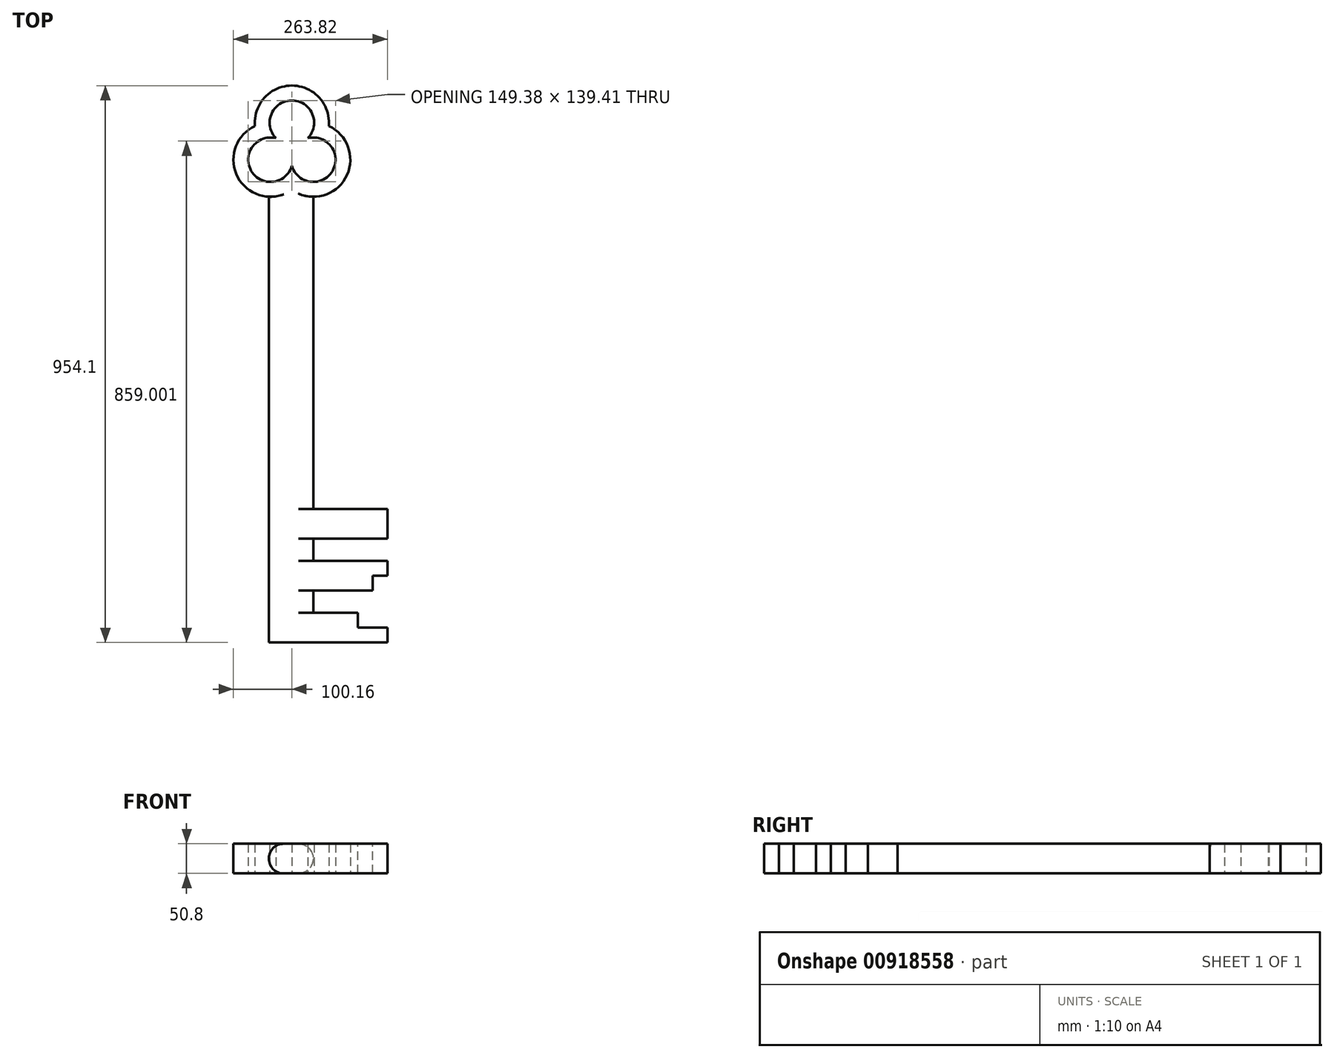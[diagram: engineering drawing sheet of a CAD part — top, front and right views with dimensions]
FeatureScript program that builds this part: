
annotation { "Feature Type Name" : "Feature", "Feature Type Description" : "" }
export const myFeature = defineFeature(function(context is Context, id is Id, definition is map)
    precondition{}
    {
        {
            var Q0;
            Q0=qCreatedBy(makeId("Top.planeOp"),FACE);
            var sketch = newSketch(context, id + "F0", { "sketchPlane" : qUnion([Q0])});
            skLineSegment(sketch, "E0.top", {"start": v(-125.96, -437.06) * mm, "end": v(-49.76, -437.06) * mm});
            skLineSegment(sketch, "E0.right", {"start": v(-49.76, 326.6) * mm, "end": v(-49.76, -208.46) * mm});
            skArc(sketch, "E1", {"start": v(-113.73, 426.98) * mm, "mid": v(-156.08, 371) * mm, "end": v(-86.42, 379.67) * mm});
            skArc(sketch, "E2", {"start": v(-86.42, 379.67) * mm, "mid": v(-16.76, 371) * mm, "end": v(-59.1, 426.98) * mm});
            skArc(sketch, "E3", {"start": v(-59.1, 426.98) * mm, "mid": v(-86.42, 491.64) * mm, "end": v(-113.73, 426.98) * mm});
            skLineSegment(sketch, "E4", {"start": v(-49.76, -437.06) * mm, "end": v(77.24, -437.06) * mm});
            skLineSegment(sketch, "E5", {"start": v(77.24, -437.06) * mm, "end": v(77.24, -386.26) * mm});
            skLineSegment(sketch, "E6", {"start": v(77.24, -386.26) * mm, "end": v(-49.76, -386.26) * mm});
            skLineSegment(sketch, "E7", {"start": v(-49.76, -348.16) * mm, "end": v(77.24, -348.16) * mm});
            skLineSegment(sketch, "E8", {"start": v(77.24, -348.16) * mm, "end": v(77.24, -297.36) * mm});
            skLineSegment(sketch, "E9", {"start": v(77.24, -297.36) * mm, "end": v(-49.76, -297.36) * mm});
            skLineSegment(sketch, "E10", {"start": v(-49.76, -259.26) * mm, "end": v(77.24, -259.26) * mm});
            skLineSegment(sketch, "E11", {"start": v(77.24, -259.26) * mm, "end": v(77.24, -208.46) * mm});
            skLineSegment(sketch, "E12", {"start": v(77.24, -208.46) * mm, "end": v(-49.76, -208.46) * mm});
            skArc(sketch, "E13", {"start": v(-149.65, 447.72) * mm, "mid": v(-185.4, 377.85) * mm, "end": v(-125.96, 326.6) * mm});
            skArc(sketch, "E14", {"start": v(-49.76, 326.6) * mm, "mid": v(12.2, 376.45) * mm, "end": v(-23.2, 447.65) * mm});
            skLineSegment(sketch, "E15.trimOffspring", {"start": v(-125.96, 326.6) * mm, "end": v(-125.96, -437.06) * mm});
            skArc(sketch, "E16.trimOffspring", {"start": v(-23.2, 447.65) * mm, "mid": v(-86.39, 517.04) * mm, "end": v(-149.65, 447.72) * mm});
            skLineSegment(sketch, "E17.trimOffspring", {"start": v(-49.76, -259.26) * mm, "end": v(-49.76, -297.36) * mm});
            skLineSegment(sketch, "E18.trimOffspring", {"start": v(-49.76, -348.16) * mm, "end": v(-49.76, -386.26) * mm});
            skLineSegment(sketch, "E19", {"start": v(-125.96, 326.6) * mm, "end": v(-49.76, 326.6) * mm, "construction": true});
            skLineSegment(sketch, "E20", {"start": v(-123.08, 390.04) * mm, "end": v(-49.76, 390.04) * mm, "construction": true});
            skLineSegment(sketch, "E21", {"start": v(-123.08, 390.04) * mm, "end": v(-86.42, 453.54) * mm, "construction": true});
            skLineSegment(sketch, "E22", {"start": v(-49.76, 390.04) * mm, "end": v(-86.42, 453.54) * mm, "construction": true});
            skSolve(sketch);
        }
        {
            var Q0;
            Q0 = qSketchRegion(id + "F0", true);
            extrude(context, id + "F1", {"entities" : qUnion([Q0]), "depth" : 50.8 * mm, "offsetDistance" : 25.4 * mm});
        }
        {
            var Q0;
            Q0=makeQuery(id+"F1.opExtrude","CAP_EDGE",EDGE,{"disambiguationData":[OSD([sQuery(id+"F0.wireOp",EDGE,"E15.trimOffspring")])],"isStart":false});
            var Q1;
            Q1=makeQuery(id+"F1.opExtrude","CAP_EDGE",EDGE,{"disambiguationData":[OSD([sQuery(id+"F0.wireOp",EDGE,"E0.right")])],"isStart":false});
            var Q2;
            Q2=makeQuery(id+"F1.opExtrude","CAP_EDGE",EDGE,{"disambiguationData":[OSD([sQuery(id+"F0.wireOp",EDGE,"E0.right")])],"isStart":true});
            var Q3;
            Q3=makeQuery(id+"F1.opExtrude","CAP_EDGE",EDGE,{"disambiguationData":[OSD([sQuery(id+"F0.wireOp",EDGE,"E15.trimOffspring")])],"isStart":true});
            var Q4;
            Q4=makeQuery(id+"F1.opExtrude","CAP_EDGE",EDGE,{"disambiguationData":[OSD([sQuery(id+"F0.wireOp",EDGE,"E17.trimOffspring")])],"isStart":true});
            var Q5;
            Q5=makeQuery(id+"F1.opExtrude","CAP_EDGE",EDGE,{"disambiguationData":[OSD([sQuery(id+"F0.wireOp",EDGE,"E18.trimOffspring")])],"isStart":true});
            var Q6;
            Q6=makeQuery(id+"F1.opExtrude","CAP_EDGE",EDGE,{"disambiguationData":[OSD([sQuery(id+"F0.wireOp",EDGE,"E18.trimOffspring")])],"isStart":false});
            var Q7;
            Q7=makeQuery(id+"F1.opExtrude","CAP_EDGE",EDGE,{"disambiguationData":[OSD([sQuery(id+"F0.wireOp",EDGE,"E17.trimOffspring")])],"isStart":false});
            fillet(context, id + "F2", {"entities" : qUnion([Q0, Q1, Q2, Q3, Q4, Q5, Q6, Q7]), "radius" : 25.4 * mm, "tangentPropagation" : true, "allowEdgeOverflow" : false});
        }
        {
            var Q0;
            Q0=makeQuery(id+"F1.opExtrude","CAP_FACE",FACE,{"disambiguationData":[OSD([sQuery(id+"F0.wireOp",EDGE,"E0.top"),sQuery(id+"F0.wireOp",EDGE,"E0.right"),sQuery(id+"F0.wireOp",EDGE,"E1"),sQuery(id+"F0.wireOp",EDGE,"E2"),sQuery(id+"F0.wireOp",EDGE,"E3"),sQuery(id+"F0.wireOp",EDGE,"E4"),sQuery(id+"F0.wireOp",EDGE,"E5"),sQuery(id+"F0.wireOp",EDGE,"E6"),sQuery(id+"F0.wireOp",EDGE,"E7"),sQuery(id+"F0.wireOp",EDGE,"E8"),sQuery(id+"F0.wireOp",EDGE,"E9"),sQuery(id+"F0.wireOp",EDGE,"E10"),sQuery(id+"F0.wireOp",EDGE,"E11"),sQuery(id+"F0.wireOp",EDGE,"E12"),sQuery(id+"F0.wireOp",EDGE,"E13"),sQuery(id+"F0.wireOp",EDGE,"E14"),sQuery(id+"F0.wireOp",EDGE,"E15.trimOffspring"),sQuery(id+"F0.wireOp",EDGE,"E16.trimOffspring"),sQuery(id+"F0.wireOp",EDGE,"E17.trimOffspring"),sQuery(id+"F0.wireOp",EDGE,"E18.trimOffspring")])],"isStart":false});
            var sketch = newSketch(context, id + "F3", { "sketchPlane" : qUnion([Q0])});
            skSolve(sketch);
        }
        {
            var Q0;
            {var subQ17=sQuery(id+"F0.wireOp",EDGE,"E1");Q0=makeQuery(id+"F3.imprint","IMPRINT",FACE,{"disambiguationData":[TD([[makeQuery(id+"F3.imprint","IMPRINT",EDGE,{"derivedFrom":makeQuery(id+"F1.opExtrude","CAP_EDGE",EDGE,{"disambiguationData":[OSD([subQ17])],"isStart":false})}),-1.0]])]});}
            var sketch = newSketch(context, id + "F4", { "sketchPlane" : qUnion([Q0])});
            skLineSegment(sketch, "E23.bottom", {"start": v(26.44, -411.66) * mm, "end": v(88.26, -411.66) * mm});
            skLineSegment(sketch, "E23.top", {"start": v(26.44, -369.46) * mm, "end": v(88.26, -369.46) * mm});
            skLineSegment(sketch, "E23.left", {"start": v(26.44, -411.66) * mm, "end": v(26.44, -369.46) * mm});
            skLineSegment(sketch, "E23.right", {"start": v(88.26, -411.66) * mm, "end": v(88.26, -369.46) * mm});
            skLineSegment(sketch, "E24.bottom", {"start": v(51.84, -322.76) * mm, "end": v(96.59, -322.76) * mm});
            skLineSegment(sketch, "E24.top", {"start": v(51.84, -354.1) * mm, "end": v(96.59, -354.1) * mm});
            skLineSegment(sketch, "E24.left", {"start": v(51.84, -322.76) * mm, "end": v(51.84, -354.1) * mm});
            skLineSegment(sketch, "E24.right", {"start": v(96.59, -322.76) * mm, "end": v(96.59, -354.1) * mm});
            skSolve(sketch);
        }
        {
            var Q0;
            Q0 = qSketchRegion(id + "F4", true);
            extrude(context, id + "F5", {"entities" : qUnion([Q0]), "operationType" : NewBodyOperationType.REMOVE, "oppositeDirection" : true, "depth" : 50.8 * mm, "offsetDistance" : 25.4 * mm});
        }
    });
